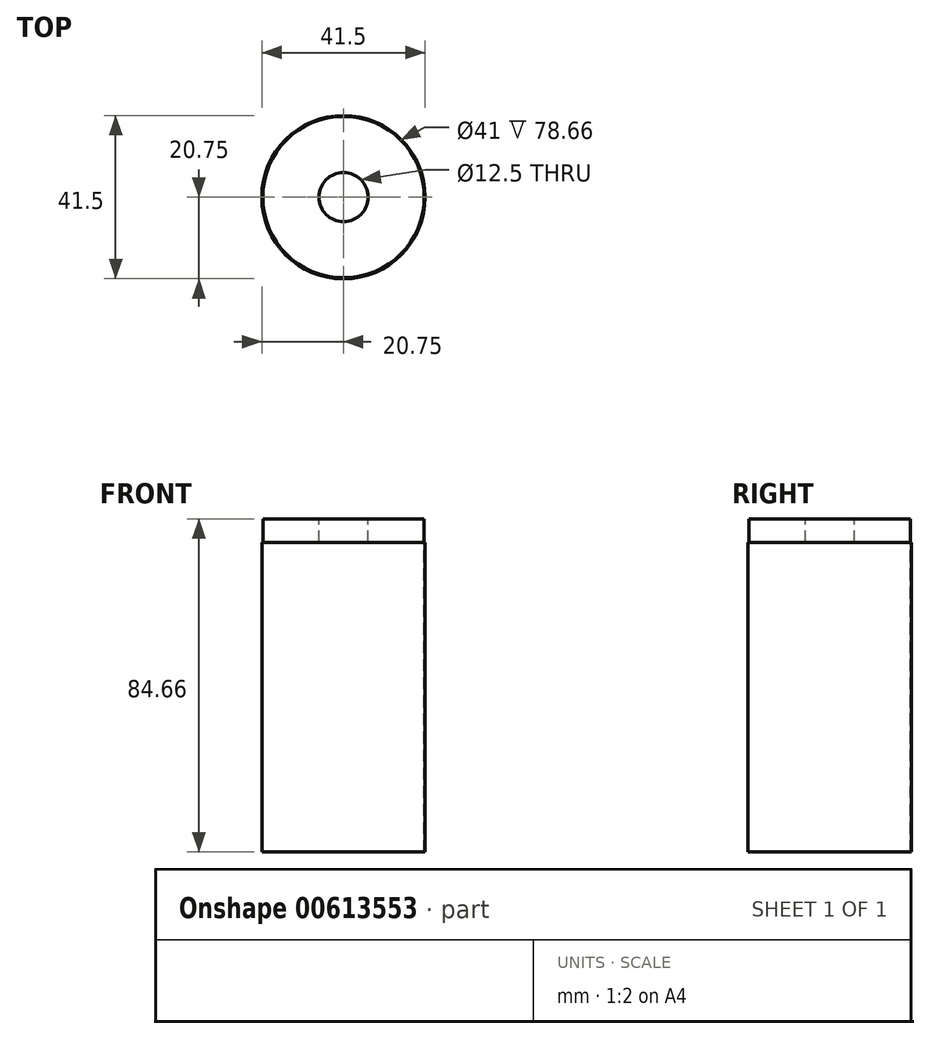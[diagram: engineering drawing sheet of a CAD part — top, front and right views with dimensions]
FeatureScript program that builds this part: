
annotation { "Feature Type Name" : "Feature", "Feature Type Description" : "" }
export const myFeature = defineFeature(function(context is Context, id is Id, definition is map)
    precondition{}
    {
        {
            var Q0;
            Q0=qCreatedBy(makeId("Top.planeOp"),FACE);
            var sketch = newSketch(context, id + "F0", { "sketchPlane" : qUnion([Q0])});
            skCircle(sketch, "E0", {"center": v(0, 0) * mm, "radius": 20.5 * mm});
            skSolve(sketch);
        }
        {
            var Q0;
            Q0 = qSketchRegion(id + "F0", true);
            extrude(context, id + "F1", {"entities" : qUnion([Q0]), "oppositeDirection" : true, "depth" : 6 * mm, "offsetDistance" : 25 * mm});
        }
        {
            var Q0;
            Q0=makeQuery(id+"F1.opExtrude","CAP_FACE",FACE,{"disambiguationData":[OSD([sQuery(id+"F0.wireOp",EDGE,"E0")])],"isStart":false});
            var sketch = newSketch(context, id + "F2", { "sketchPlane" : qUnion([Q0])});
            skCircle(sketch, "E1", {"center": v(0, 0) * mm, "radius": 20.75 * mm});
            skSolve(sketch);
        }
        {
            var Q0;
            Q0=makeQuery(id+"F2.imprint","IMPRINT",FACE,{"disambiguationData":[TD([[makeQuery(id+"F2.imprint","IMPRINT",EDGE,{"derivedFrom":sQuery(id+"F2.wireOp",EDGE,"E1")}),1.0]])]});
            extrude(context, id + "F3", {"entities" : qUnion([Q0]), "depth" : 38.66 * mm, "offsetDistance" : 25 * mm});
        }
        {
            var Q0;
            Q0=makeQuery(id+"F1.opExtrude","CAP_FACE",FACE,{"disambiguationData":[OSD([sQuery(id+"F0.wireOp",EDGE,"E0")])],"isStart":true});
            var sketch = newSketch(context, id + "F4", { "sketchPlane" : qUnion([Q0])});
            skCircle(sketch, "E2", {"center": v(0, 0) * mm, "radius": 6 * mm});
            skSolve(sketch);
        }
        {
            var Q0;
            Q0=makeQuery(id+"F3.opExtrude","CAP_FACE",FACE,{"disambiguationData":[OSD([sQuery(id+"F0.wireOp",EDGE,"E0"),sQuery(id+"F2.wireOp",EDGE,"E1")])],"isStart":false});
            extrude(context, id + "F5", {"entities" : qUnion([Q0]), "operationType" : NewBodyOperationType.ADD, "depth" : 40 * mm, "offsetDistance" : 25 * mm});
        }
        {
            var Q0;
            Q0=sQuery(id+"F4.wireOp",VERTEX,"E2.center");
            var Q1;
            Q1=makeQuery(id+"F1.opExtrude","SWEPT_BODY",BODY,{"disambiguationData":[OSD([sQuery(id+"F0.wireOp",EDGE,"E0")])]});
            var Q2;
            Q2=makeQuery(id+"F3.opExtrude","SWEPT_BODY",BODY,{"disambiguationData":[OSD([sQuery(id+"F0.wireOp",EDGE,"E0"),sQuery(id+"F2.wireOp",EDGE,"E1")])]});
            hole(context, id + "F6", {"style" : HoleStyle.SIMPLE, "endStyle" : HoleEndStyle.THROUGH, "standardTappedOrClearance" : lookupTablePath({ "standard" : "ISO", "engagement" : "75%", "pitch" : "1.5 mm", "size" : "M14", "type" : "Tapped" }), "standardBlindInLast" : lookupTablePath({ "standard" : "ISO", "engagement" : "75%", "pitch" : "1.5 mm", "size" : "M14", "type" : "Tapped" }), "holeDiameter" : 12.5 * mm, "majorDiameter" : 14 * mm, "showTappedDepth" : true, "tappedDepth" : 40 * mm, "tapClearance" : 3, "startFromSketch" : true, "locations" : qUnion([Q0]), "scope" : qUnion([Q1, Q2])});
        }
    });
